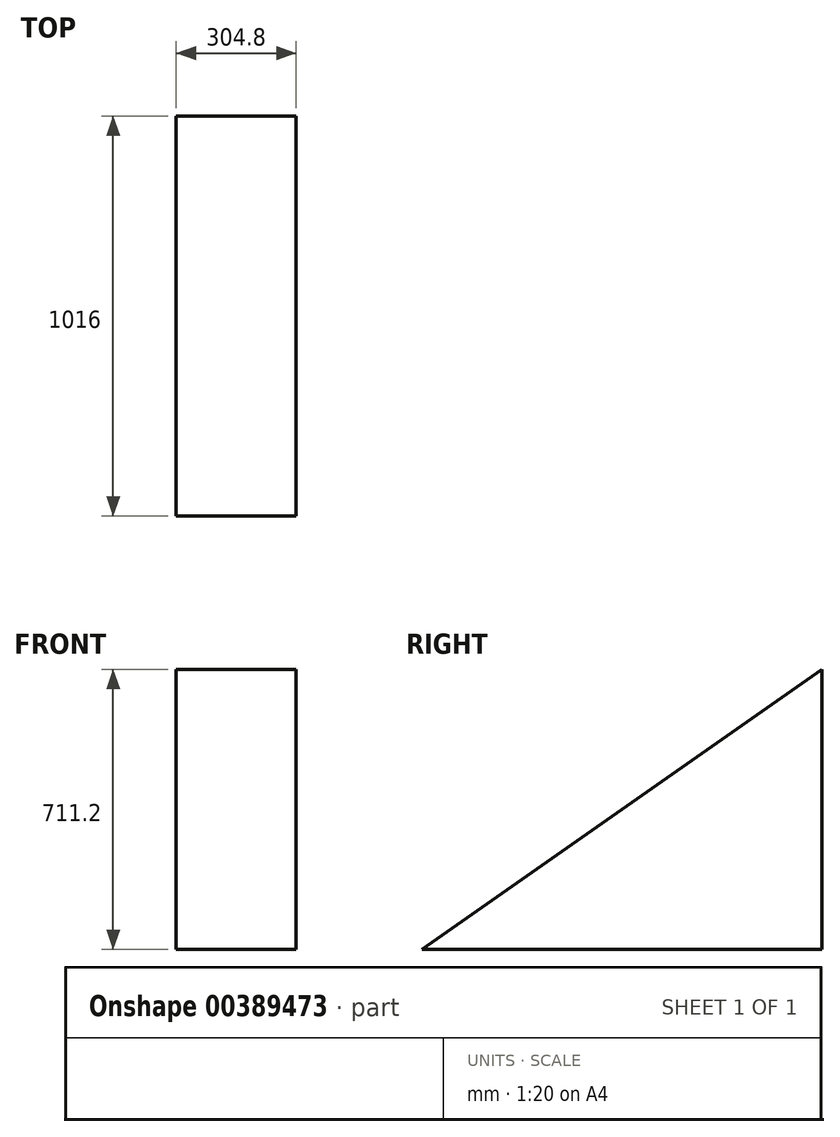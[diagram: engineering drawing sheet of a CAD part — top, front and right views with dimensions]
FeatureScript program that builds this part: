
annotation { "Feature Type Name" : "Feature", "Feature Type Description" : "" }
export const myFeature = defineFeature(function(context is Context, id is Id, definition is map)
    precondition{}
    {
        {
            var Q0;
            Q0=qCreatedBy(makeId("Right.planeOp"),FACE);
            var sketch = newSketch(context, id + "F0", { "sketchPlane" : qUnion([Q0])});
            skLineSegment(sketch, "E0", {"start": v(0, 0) * mm, "end": v(-1016, 0) * mm});
            skLineSegment(sketch, "E1", {"start": v(0, 711.2) * mm, "end": v(0, 0) * mm});
            skLineSegment(sketch, "E2", {"start": v(0, 711.2) * mm, "end": v(-1016, 0) * mm});
            skSolve(sketch);
        }
        {
            var Q0;
            Q0=makeQuery(id+"F0.imprint","IMPRINT",FACE,{"disambiguationData":[TD([[makeQuery(id+"F0.imprint","IMPRINT",EDGE,{"derivedFrom":sQuery(id+"F0.wireOp",EDGE,"E0")}),-1.0]])]});
            extrude(context, id + "F1", {"entities" : qUnion([Q0]), "depth" : 304.8 * mm});
        }
    });
